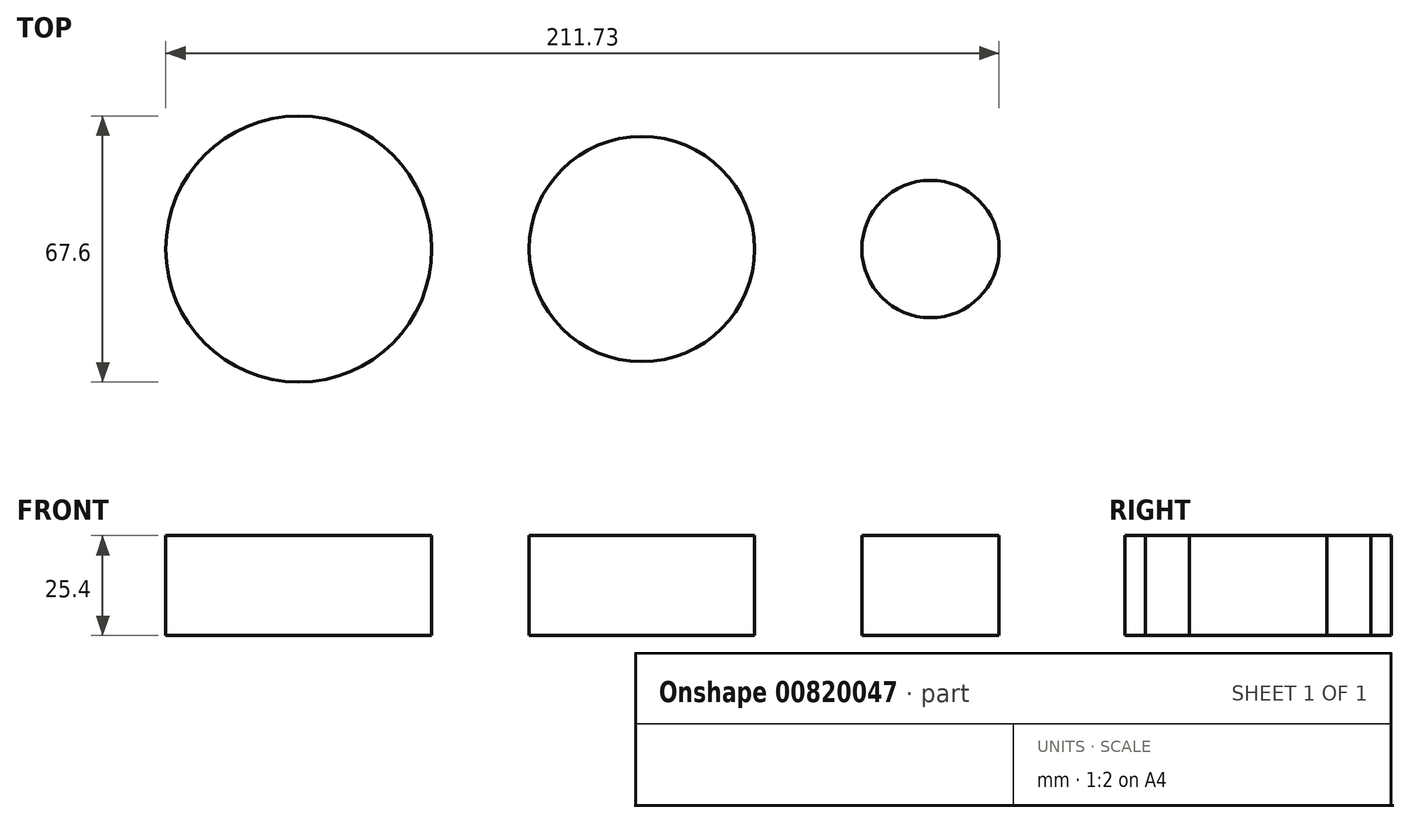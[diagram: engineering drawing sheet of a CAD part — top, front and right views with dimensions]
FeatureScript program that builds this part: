
annotation { "Feature Type Name" : "Feature", "Feature Type Description" : "" }
export const myFeature = defineFeature(function(context is Context, id is Id, definition is map)
    precondition{}
    {
        {
            var Q0;
            Q0=qCreatedBy(makeId("Top.planeOp"),FACE);
            var sketch = newSketch(context, id + "F0", { "sketchPlane" : qUnion([Q0])});
            skCircle(sketch, "E0", {"center": v(-87.16, 0) * mm, "radius": 33.8 * mm});
            skCircle(sketch, "E1", {"center": v(73.34, 0) * mm, "radius": 17.45 * mm});
            skCircle(sketch, "E2", {"center": v(0, 0) * mm, "radius": 28.63 * mm});
            skSolve(sketch);
        }
        {
            var Q0;
            Q0=makeQuery(id+"F0.imprint","IMPRINT",FACE,{"disambiguationData":[TD([[makeQuery(id+"F0.imprint","IMPRINT",EDGE,{"derivedFrom":sQuery(id+"F0.wireOp",EDGE,"E0")}),1.0]])]});
            var Q1;
            Q1=makeQuery(id+"F0.imprint","IMPRINT",FACE,{"disambiguationData":[TD([[makeQuery(id+"F0.imprint","IMPRINT",EDGE,{"derivedFrom":sQuery(id+"F0.wireOp",EDGE,"E2")}),1.0]])]});
            var Q2;
            Q2=makeQuery(id+"F0.imprint","IMPRINT",FACE,{"disambiguationData":[TD([[makeQuery(id+"F0.imprint","IMPRINT",EDGE,{"derivedFrom":sQuery(id+"F0.wireOp",EDGE,"E1")}),1.0]])]});
            extrude(context, id + "F1", {"entities" : qUnion([Q0, Q1, Q2]), "depth" : 25.4 * mm, "offsetDistance" : 25.4 * mm});
        }
    });
